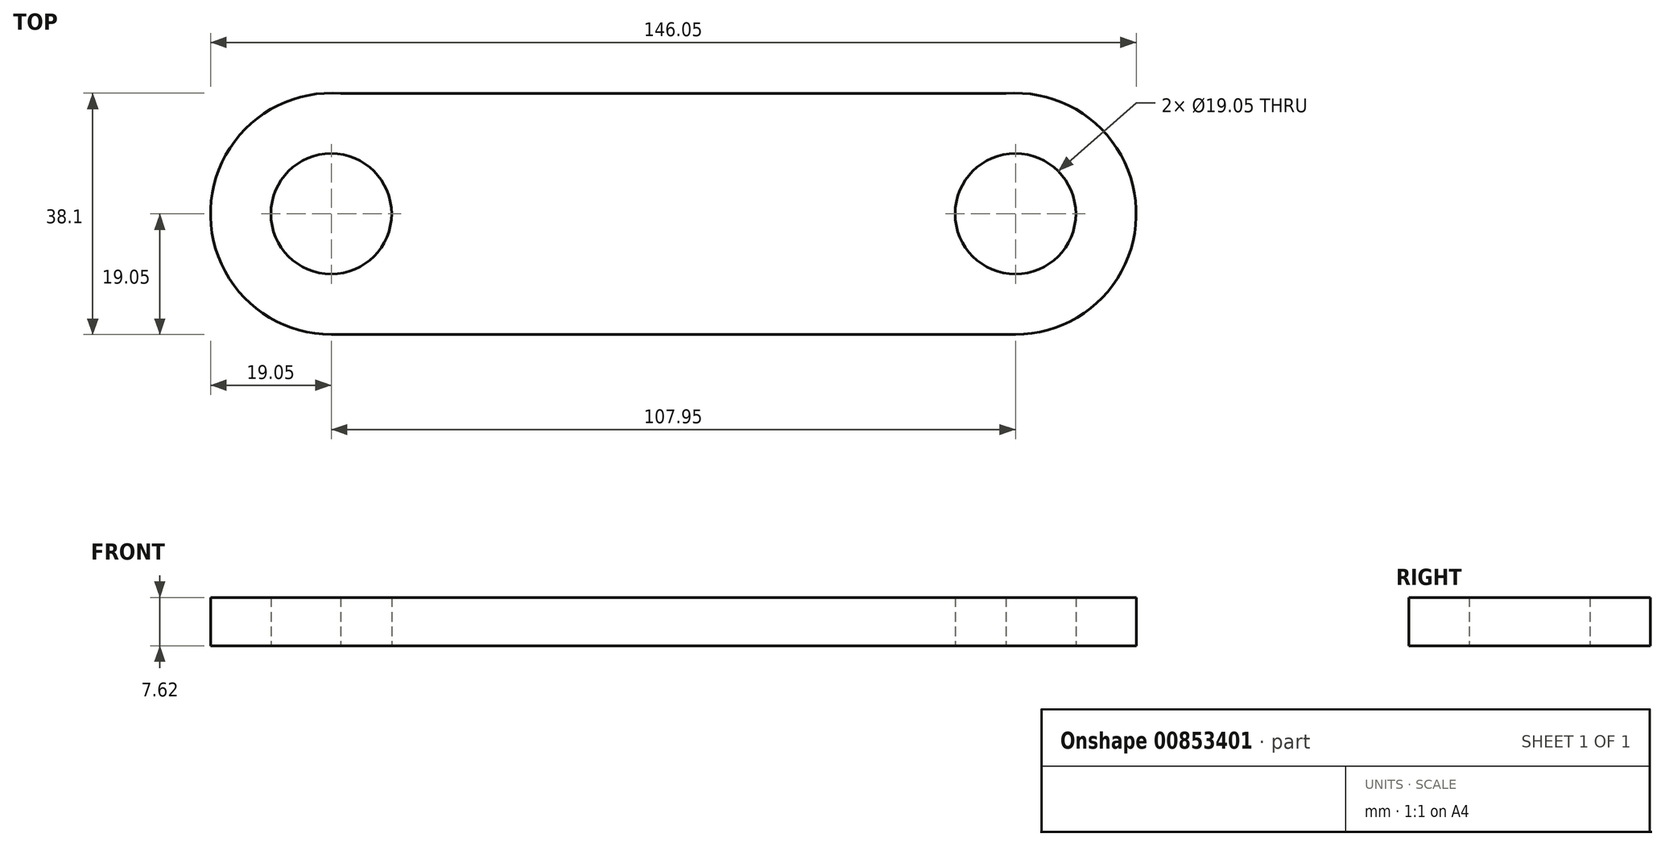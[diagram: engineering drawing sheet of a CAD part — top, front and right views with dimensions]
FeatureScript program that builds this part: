
annotation { "Feature Type Name" : "Feature", "Feature Type Description" : "" }
export const myFeature = defineFeature(function(context is Context, id is Id, definition is map)
    precondition{}
    {
        {
            var Q0;
            Q0=qCreatedBy(makeId("Top.planeOp"),FACE);
            var sketch = newSketch(context, id + "F0", { "sketchPlane" : qUnion([Q0])});
            skArc(sketch, "E0", {"start": v(0, -19.05) * mm, "mid": v(19.04, 0.75) * mm, "end": v(-1.5, 19) * mm});
            skArc(sketch, "E1", {"start": v(-106.45, 19) * mm, "mid": v(-126.99, 0.75) * mm, "end": v(-107.95, -19.05) * mm});
            skLineSegment(sketch, "E2", {"start": v(-106.45, 19) * mm, "end": v(0, 19) * mm});
            skLineSegment(sketch, "E3", {"start": v(0, -19.05) * mm, "end": v(-107.95, -19.05) * mm});
            skCircle(sketch, "E4", {"center": v(-107.95, 0) * mm, "radius": 9.53 * mm});
            skCircle(sketch, "E5", {"center": v(0, 0) * mm, "radius": 9.53 * mm});
            skSolve(sketch);
        }
        {
            var Q0;
            Q0 = qSketchRegion(id + "F0", true);
            extrude(context, id + "F1", {"entities" : qUnion([Q0]), "depth" : 7.62 * mm, "offsetDistance" : 25.4 * mm});
        }
    });
